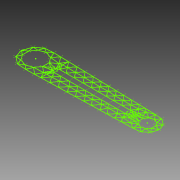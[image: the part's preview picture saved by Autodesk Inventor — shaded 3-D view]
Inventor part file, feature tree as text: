
AUTODESK INVENTOR PART (.ipt)
format: ipt  version: 2014 (Build 180170000, 170)  size: 162,304 bytes
history: native  units: mm
features: sketch x1
ambient origin geometry x8: Origin, YZ Plane, XZ Plane, XY Plane, X Axis, Y Axis, Z Axis, Center Point
feature tree (1):
  sketch  "Sketch1"
